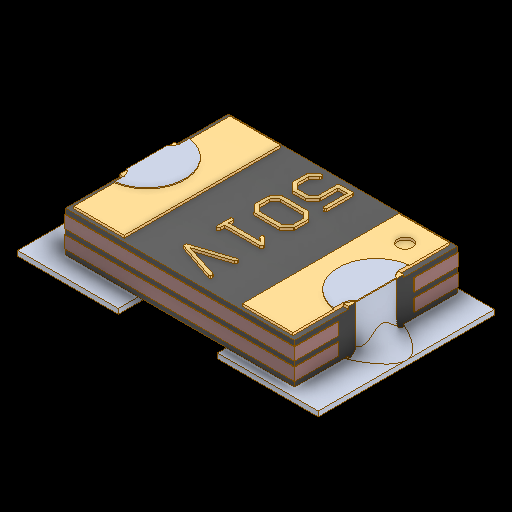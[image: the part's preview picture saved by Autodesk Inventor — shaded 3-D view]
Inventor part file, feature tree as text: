
AUTODESK INVENTOR PART (.ipt)
format: ipt  version: 2023 (Build 270158000, 158)  size: 395,776 bytes
history: native  units: in
note: dims shown in document units (in); Inventor stores cm internally (conversion verified against a paired STEP export)
features: mirror x1
ambient origin geometry x8: Origin, YZ Plane, XZ Plane, XY Plane, X Axis, Y Axis, Z Axis, Center Point
bodies: Solid1 (feature_tree)
feature tree (1):
  mirror  "Mirror5"
